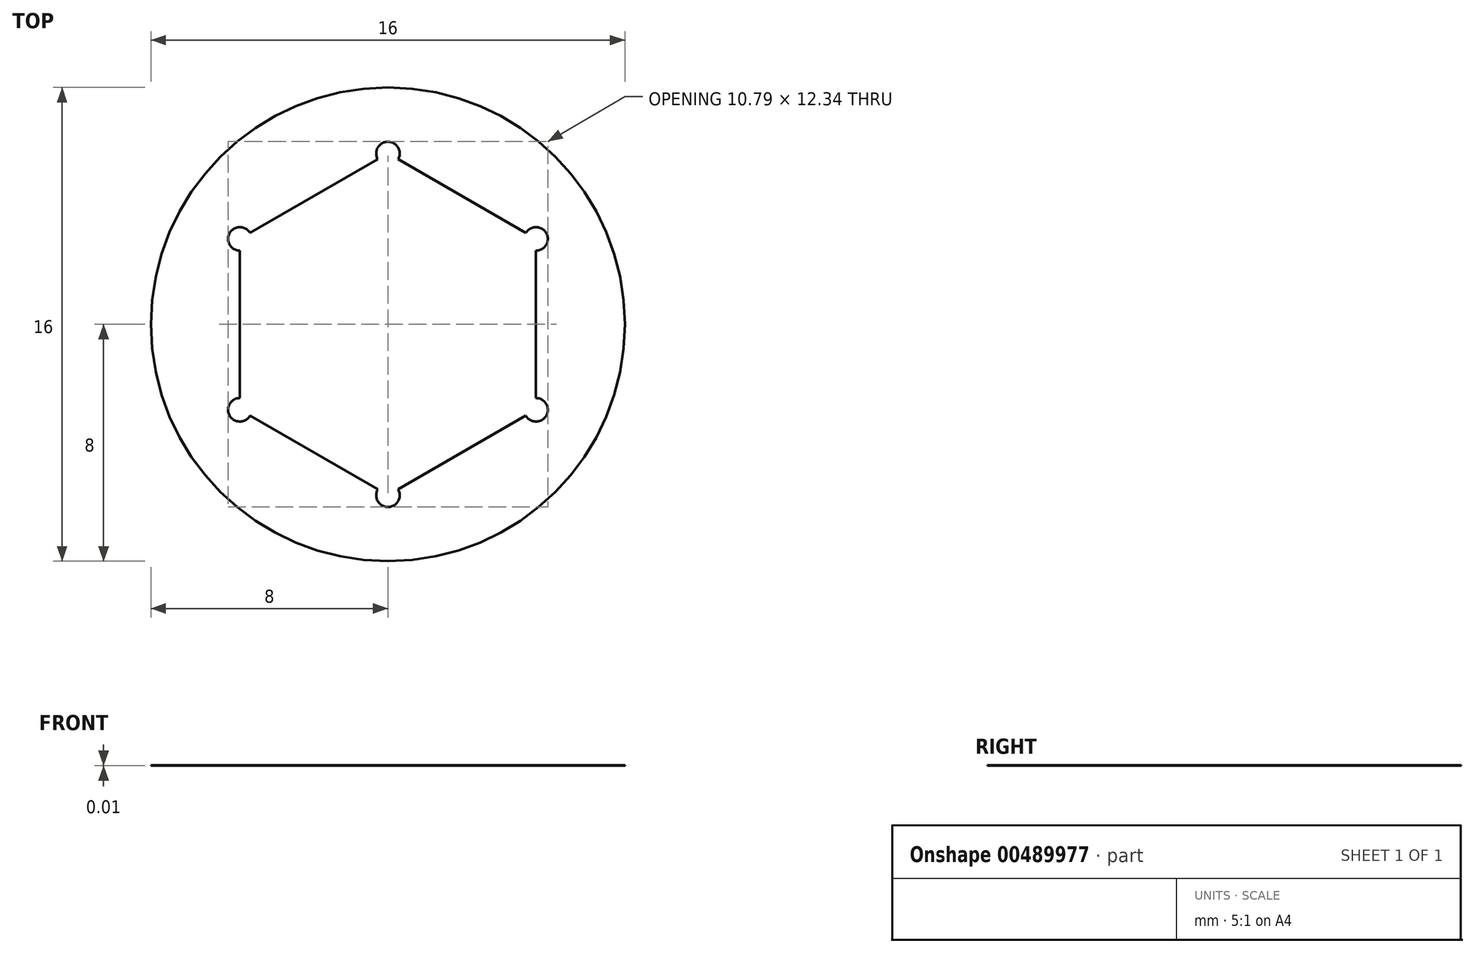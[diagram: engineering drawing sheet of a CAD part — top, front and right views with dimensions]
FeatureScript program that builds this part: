
annotation { "Feature Type Name" : "Feature", "Feature Type Description" : "" }
export const myFeature = defineFeature(function(context is Context, id is Id, definition is map)
    precondition{}
    {
        {
            var Q0;
            Q0=qCreatedBy(makeId("Top.planeOp"),FACE);
            var sketch = newSketch(context, id + "F0", { "sketchPlane" : qUnion([Q0])});
            skCircle(sketch, "E0.cCircle", {"center": v(0, 0) * mm, "radius": 5.77 * mm, "construction": true});
            skLineSegment(sketch, "E0.0", {"start": v(0.34, 5.58) * mm, "end": v(4.66, 3.09) * mm});
            skLineSegment(sketch, "E0.1", {"start": v(5, 2.49) * mm, "end": v(5, -2.49) * mm});
            skLineSegment(sketch, "E0.2", {"start": v(4.66, -3.09) * mm, "end": v(0.34, -5.58) * mm});
            skLineSegment(sketch, "E0.3", {"start": v(-0.34, -5.58) * mm, "end": v(-4.66, -3.09) * mm});
            skLineSegment(sketch, "E0.4", {"start": v(-5, -2.49) * mm, "end": v(-5, 2.49) * mm});
            skLineSegment(sketch, "E0.5", {"start": v(-4.66, 3.09) * mm, "end": v(-0.34, 5.58) * mm});
            skCircle(sketch, "E1", {"center": v(0, 0) * mm, "radius": 8 * mm});
            skArc(sketch, "E2", {"start": v(0.34, 5.58) * mm, "mid": v(0, 6.17) * mm, "end": v(-0.34, 5.58) * mm});
            skArc(sketch, "E3.1.0", {"start": v(-4.66, 3.09) * mm, "mid": v(-5.34, 3.09) * mm, "end": v(-5, 2.49) * mm});
            skArc(sketch, "E3.2.0", {"start": v(-5, -2.49) * mm, "mid": v(-5.34, -3.09) * mm, "end": v(-4.66, -3.09) * mm});
            skArc(sketch, "E3.3.0", {"start": v(-0.34, -5.58) * mm, "mid": v(0, -6.17) * mm, "end": v(0.34, -5.58) * mm});
            skArc(sketch, "E3.4.0", {"start": v(4.66, -3.09) * mm, "mid": v(5.34, -3.09) * mm, "end": v(5, -2.49) * mm});
            skArc(sketch, "E3.5.0", {"start": v(5, 2.49) * mm, "mid": v(5.34, 3.09) * mm, "end": v(4.66, 3.09) * mm});
            skSolve(sketch);
        }
        {
            var Q0;
            Q0=makeQuery(id+"F0.imprint","IMPRINT",FACE,{"disambiguationData":[TD([[makeQuery(id+"F0.imprint","IMPRINT",EDGE,{"derivedFrom":sQuery(id+"F0.wireOp",EDGE,"E0.0")}),1.0]])]});
            extrude(context, id + "F1", {"entities" : qUnion([Q0]), "depth" : 3 / 203.2 * mm});
        }
    });
